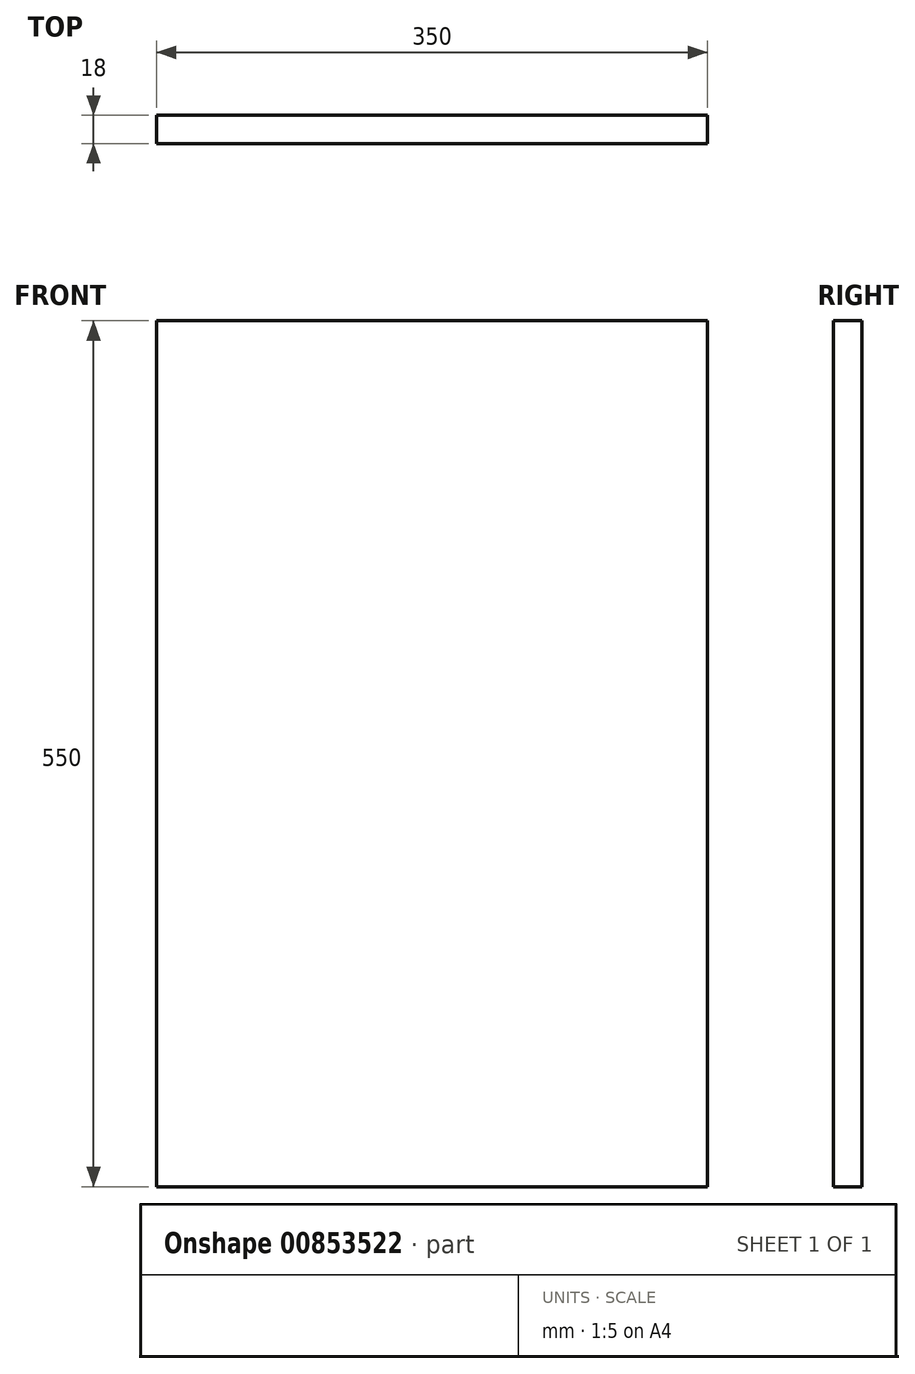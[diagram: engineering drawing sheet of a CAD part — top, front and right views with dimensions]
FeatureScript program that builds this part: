
annotation { "Feature Type Name" : "Feature", "Feature Type Description" : "" }
export const myFeature = defineFeature(function(context is Context, id is Id, definition is map)
    precondition{}
    {
        {
            var Q0;
            Q0=qCreatedBy(makeId("Front.planeOp"),FACE);
            var sketch = newSketch(context, id + "F0", { "sketchPlane" : qUnion([Q0])});
            skLineSegment(sketch, "E0.bottom", {"start": v(175, 275) * mm, "end": v(-175, 275) * mm});
            skLineSegment(sketch, "E0.top", {"start": v(175, -275) * mm, "end": v(-175, -275) * mm});
            skLineSegment(sketch, "E0.left", {"start": v(175, 275) * mm, "end": v(175, -275) * mm});
            skLineSegment(sketch, "E0.right", {"start": v(-175, 275) * mm, "end": v(-175, -275) * mm});
            skPoint(sketch, "E0.middle", {"position": v(0, 0) * mm});
            skSolve(sketch);
        }
        {
            var Q0;
            Q0 = qSketchRegion(id + "F0", true);
            extrude(context, id + "F1", {"entities" : qUnion([Q0]), "depth" : 18 * mm, "offsetDistance" : 25 * mm});
        }
    });
